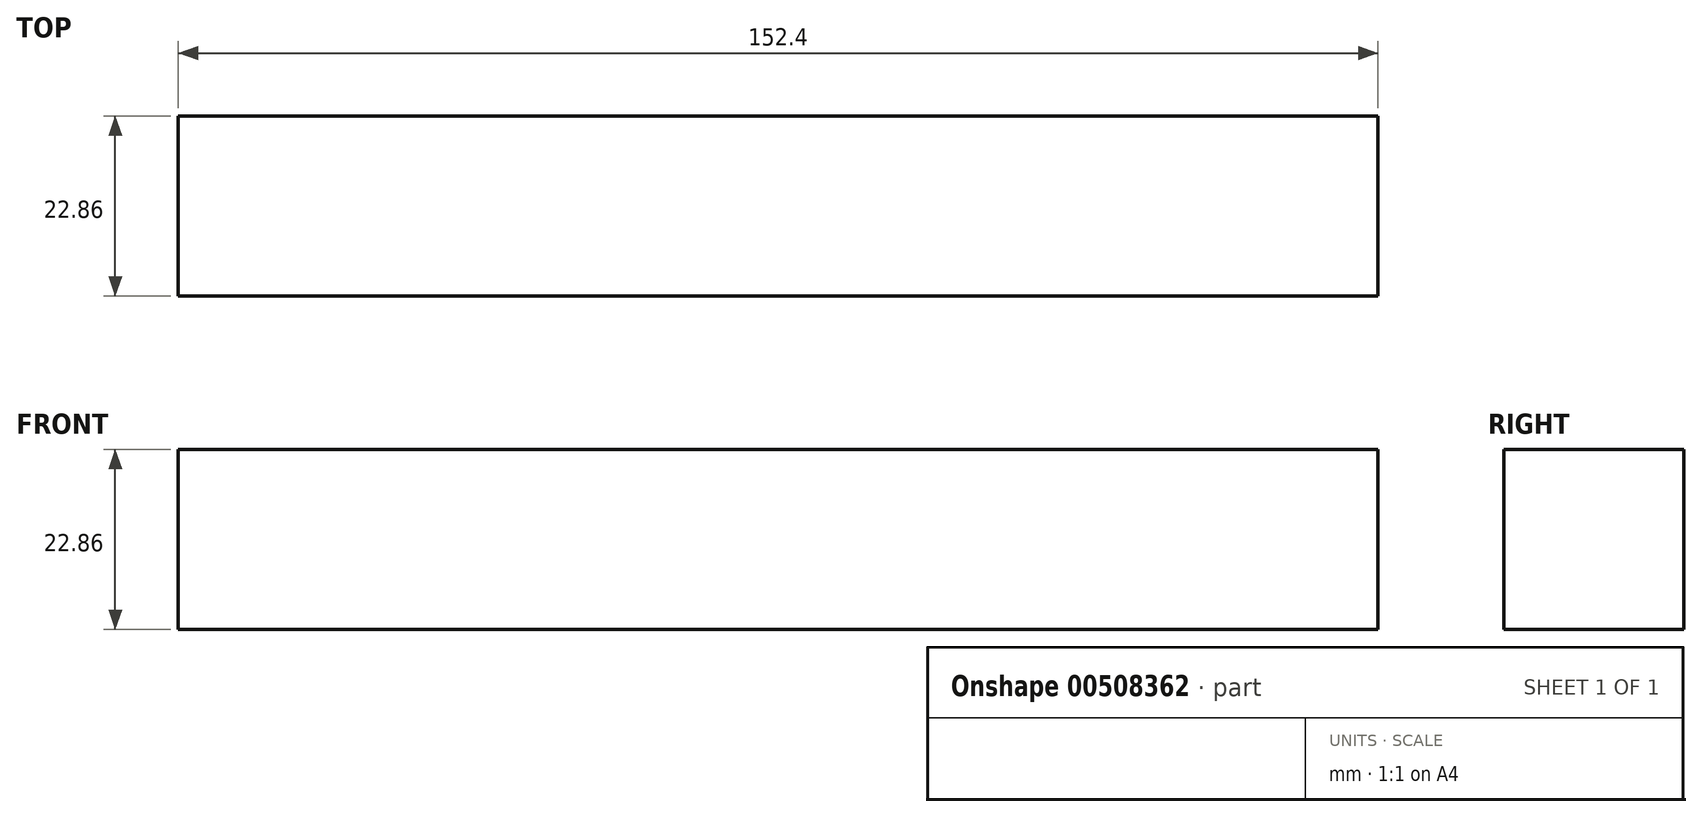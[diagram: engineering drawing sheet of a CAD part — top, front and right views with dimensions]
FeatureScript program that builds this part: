
annotation { "Feature Type Name" : "Feature", "Feature Type Description" : "" }
export const myFeature = defineFeature(function(context is Context, id is Id, definition is map)
    precondition{}
    {
        {
            var Q0;
            Q0=qCreatedBy(makeId("Top.planeOp"),FACE);
            var sketch = newSketch(context, id + "F0", { "sketchPlane" : qUnion([Q0])});
            skLineSegment(sketch, "E0.bottom", {"start": v(-78.95, 14.77) * mm, "end": v(73.45, 14.77) * mm});
            skLineSegment(sketch, "E0.top", {"start": v(-78.95, -8.1) * mm, "end": v(73.45, -8.1) * mm});
            skLineSegment(sketch, "E0.left", {"start": v(-78.95, 14.77) * mm, "end": v(-78.95, -8.1) * mm});
            skLineSegment(sketch, "E0.right", {"start": v(73.45, 14.77) * mm, "end": v(73.45, -8.1) * mm});
            skSolve(sketch);
        }
        {
            var Q0;
            Q0=makeQuery(id+"F0.imprint","IMPRINT",FACE,{"disambiguationData":[TD([[makeQuery(id+"F0.imprint","IMPRINT",EDGE,{"derivedFrom":sQuery(id+"F0.wireOp",EDGE,"E0.bottom")}),-1.0]])]});
            extrude(context, id + "F1", {"entities" : qUnion([Q0]), "depth" : 22.86 * mm});
        }
    });
